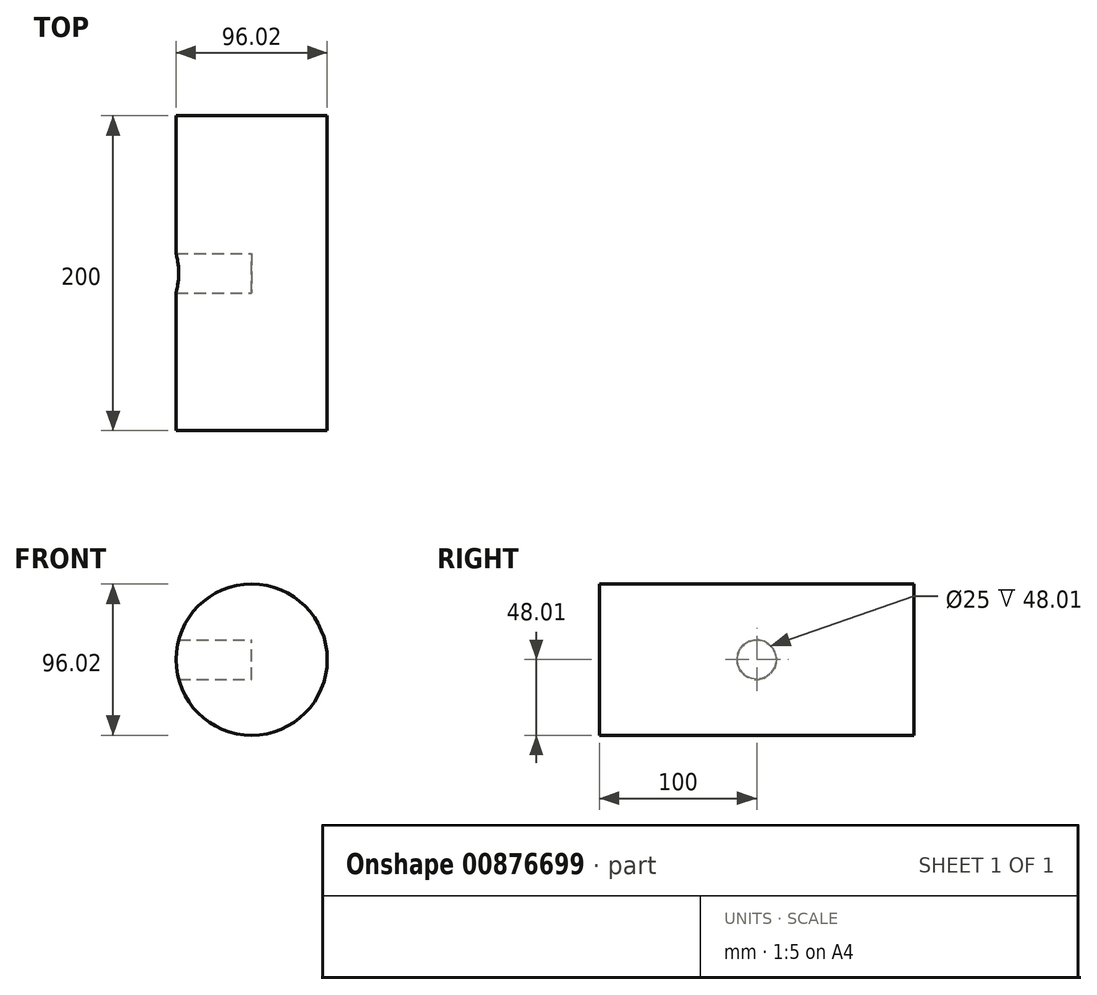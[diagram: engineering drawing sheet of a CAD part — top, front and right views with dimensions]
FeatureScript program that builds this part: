
annotation { "Feature Type Name" : "Feature", "Feature Type Description" : "" }
export const myFeature = defineFeature(function(context is Context, id is Id, definition is map)
    precondition{}
    {
        {
            var Q0;
            Q0=qCreatedBy(makeId("Front.planeOp"),FACE);
            var sketch = newSketch(context, id + "F0", { "sketchPlane" : qUnion([Q0])});
            skCircle(sketch, "E0", {"center": v(0, 0) * mm, "radius": 48 * mm});
            skSolve(sketch);
        }
        {
            var Q0;
            Q0=makeQuery(id+"F0.imprint","IMPRINT",FACE,{"disambiguationData":[TD([[makeQuery(id+"F0.imprint","IMPRINT",EDGE,{"derivedFrom":sQuery(id+"F0.wireOp",EDGE,"E0")}),1.0]])]});
            extrude(context, id + "F1", {"entities" : qUnion([Q0]), "depth" : 200 * mm, "offsetDistance" : 25 * mm});
        }
        {
            var Q0;
            Q0=qCreatedBy(makeId("Right.planeOp"),FACE);
            var sketch = newSketch(context, id + "F2", { "sketchPlane" : qUnion([Q0])});
            skPoint(sketch, "E1", {"position": v(-100, 0) * mm});
            skSolve(sketch);
        }
        {
            var Q0;
            Q0=sQuery(id+"F2.wireOp",VERTEX,"E1");
            var Q1;
            Q1=makeQuery(id+"F1.opExtrude","SWEPT_BODY",BODY,{"disambiguationData":[OSD([sQuery(id+"F0.wireOp",EDGE,"E0")])]});
            hole(context, id + "F3", {"style" : HoleStyle.SIMPLE, "endStyle" : HoleEndStyle.BLIND, "holeDiameter" : 25 * mm, "majorDiameter" : 5 * mm, "holeDepth" : 60 * mm, "isTappedThrough" : true, "tappedDepth" : 12 * mm, "tapClearance" : 3, "locations" : qUnion([Q0]), "scope" : qUnion([Q1])});
        }
    });
